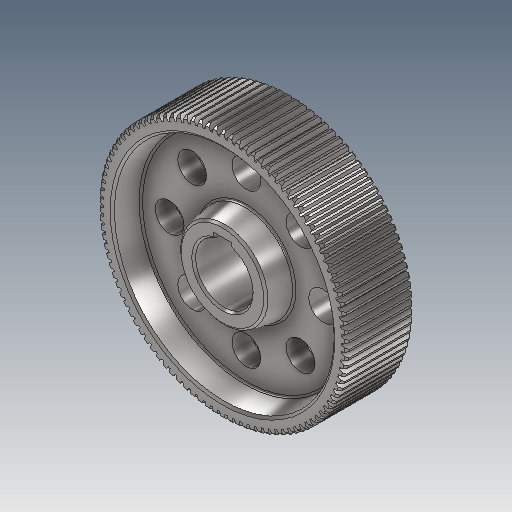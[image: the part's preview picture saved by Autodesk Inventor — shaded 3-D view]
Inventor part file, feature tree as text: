
AUTODESK INVENTOR PART (.ipt)
format: ipt  version: 2025 (Build 290162000, 162)  size: 1,378,304 bytes
history: native  units: mm (DEFAULTED — no unit token found)
features: sketch x6, extrude x5, plane x3, other x3, mirror x2, chamfer x1, fillet x1
ambient origin geometry x8: Origin, YZ Plane, XZ Plane, XY Plane, X Axis, Y Axis, Z Axis, Center Point
bodies: Solid1 (feature_tree)
feature tree (21):
  extrude  "Extrusion1"  Depth=70.0mm TaperAngle=0.0deg
  plane  "Work Plane2"
  plane  "Work Plane8"
  plane  "Work Plane9"
  other  "正齿轮"
  extrude  "拉伸2"  Depth=10.0mm TaperAngle=0.0deg
  extrude  "拉伸3"  Depth=0.307999mm TaperAngle=0.0deg
  mirror  "镜像1"
  extrude  "拉伸4"  TaperAngle=0.0deg  [1 undecoded]
  chamfer  "倒角1"  [1 undecoded]
  other  "轮毂键槽"
  fillet  "圆角1"  Radius=60.0mm
  extrude  "拉伸5"  Depth=18.0mm
  mirror  "镜像2"
  sketch  "Sketch1"  dims[d0=260.0mm d1=70.0mm d2=0.0mm]
  other  "Srf1"
  sketch  "草图3"  dims[d16=166.25mm d17=0.0mm d34=0.307999mm]
  sketch  "草图4"  dims[d39=0.0mm d41=0.0mm]
  sketch  "草图5"  dims[d43=166.25mm]
  sketch  "草图 - 环形阵列1"  dims[d3=255.0mm d4=10.0mm d5=0.0mm]
  sketch  "草图6"  dims[d46=166.25mm d47=0.0mm d48=0.0mm d49=60.0mm d50=18.0mm d51=11.0mm d52=18.0mm d53=0.0mm d54=90.0mm d55=230.0mm d56=25.0mm d57=-2.007129mm d58=30.0mm d60=80.0mm d62=360.0deg d64=70.0mm d65=0.0mm d66=2.0mm d67=2.0mm d68=45.0deg d69=2.0mm d70=160.0mm d71=2.5mm d72=70.0mm d73=-7.853982mm d74=2.5mm]
note: 2 required parameter values undecoded (feature->parameter linkage not recoverable at this tier; creation-order binding heuristic only, values carry confidence <= 0.55)
